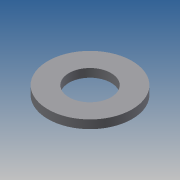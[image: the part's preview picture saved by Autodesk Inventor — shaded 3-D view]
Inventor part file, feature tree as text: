
AUTODESK INVENTOR PART (.ipt)
format: ipt  version: 2013 (Build 170138000, 138)  size: 72,704 bytes
history: native  units: mm
features: extrude x1, sketch x1
ambient origin geometry x8: Origin, YZ Plane, XZ Plane, XY Plane, X Axis, Y Axis, Z Axis, Center Point
bodies: Solid1 (feature_tree)
feature tree (2):
  extrude  "Extrusion1"  Depth=16.0mm
  sketch  "Sketch1"  dims[d0=8.0mm d2=16.0mm d3=1.6mm d4=0.0mm]
